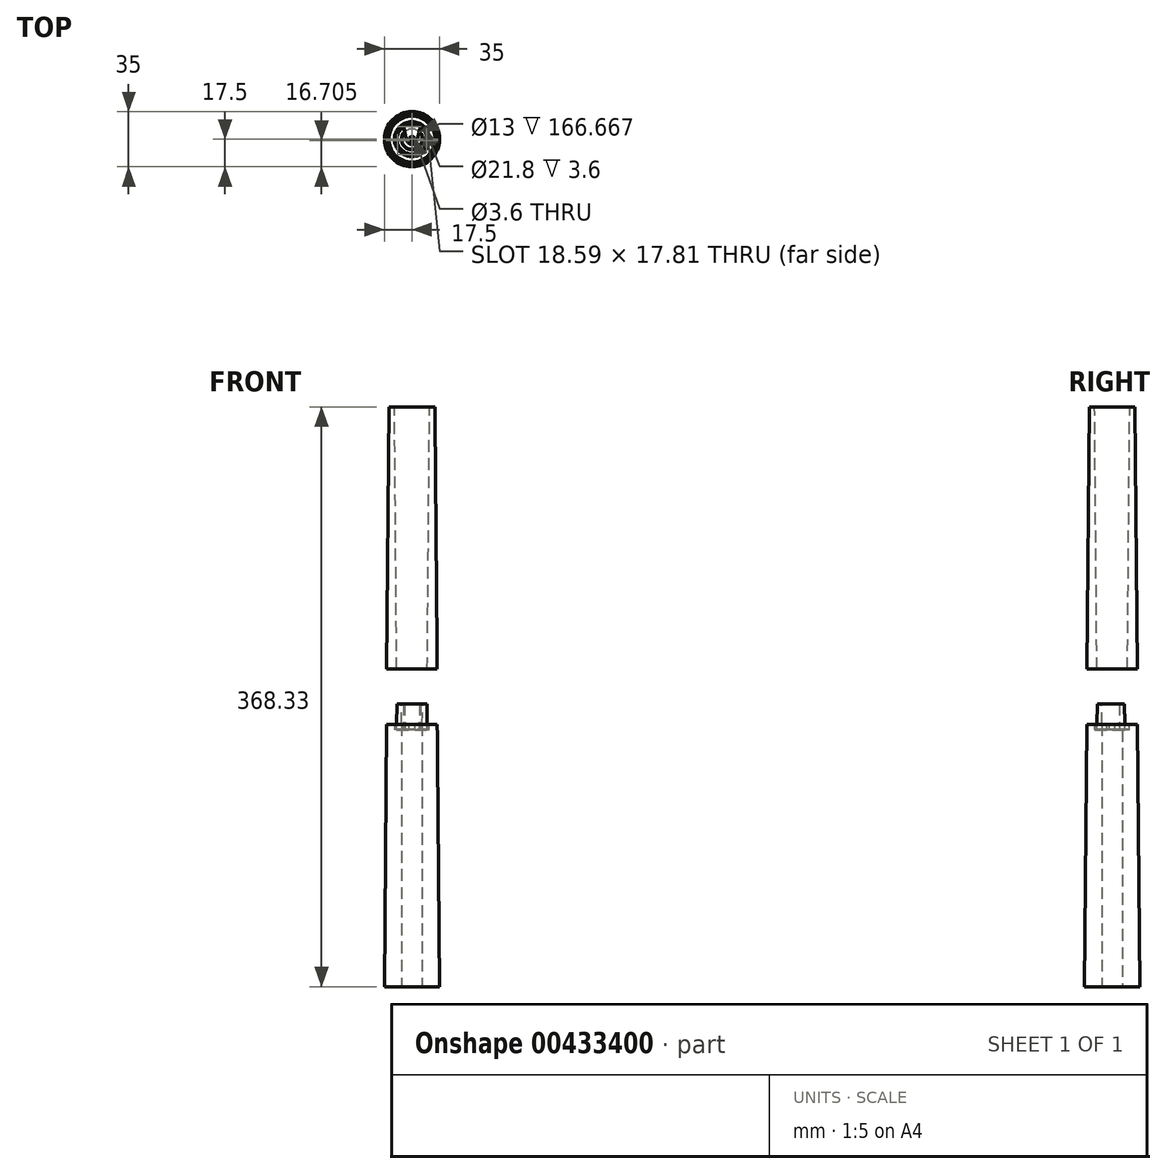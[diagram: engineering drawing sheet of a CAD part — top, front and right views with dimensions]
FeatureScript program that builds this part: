
annotation { "Feature Type Name" : "Feature", "Feature Type Description" : "" }
export const myFeature = defineFeature(function(context is Context, id is Id, definition is map)
    precondition{}
    {
        {
            assignVariable(context, id + "F0", {"name" : "RodLength", "anyValue" : 500 * mm});
        }
        {
            assignVariable(context, id + "F1", {"name" : "NubDepth", "anyValue" : 13 * mm});
        }
        {
            assignVariable(context, id + "F2", {"name" : "EjectorSupportRingDepth", "anyValue" : 3.2 * mm});
        }
        {
            var Q0;
            Q0=qCreatedBy(makeId("Top.planeOp"),FACE);
            var sketch = newSketch(context, id + "F3", { "sketchPlane" : qUnion([Q0])});
            skCircle(sketch, "E0", {"center": v(0, 0) * mm, "radius": 6.5 * mm});
            skCircle(sketch, "E1", {"center": v(0, 0) * mm, "radius": 17.5 * mm});
            skSolve(sketch);
        }
        {
            var Q0;
            Q0=qCreatedBy(makeId("Top.planeOp"),FACE);
            cPlane(context, id + "F4", {"entities" : qUnion([Q0]), "cplaneType" : CPlaneType.OFFSET, "offset" : getVariable(context, 'RodLength') / 3, "width" : 150 * mm, "height" : 150 * mm});
        }
        {
            var Q0;
            Q0=makeQuery(id+"F3.imprint","IMPRINT",FACE,{"disambiguationData":[TD([[makeQuery(id+"F3.imprint","IMPRINT",EDGE,{"derivedFrom":sQuery(id+"F3.wireOp",EDGE,"E0")}),-1.0]])]});
            var Q1;
            Q1=makeQuery(id+"F3.imprint","IMPRINT",FACE,{"disambiguationData":[TD([[makeQuery(id+"F3.imprint","IMPRINT",EDGE,{"derivedFrom":sQuery(id+"F3.wireOp",EDGE,"E0")}),1.0]])]});
            extrude(context, id + "F5", {"entities" : qUnion([Q0, Q1]), "depth" : getVariable(context, 'RodLength') / 3, "hasDraft" : true, "draftAngle" : .5 * degree, "draftPullDirection" : true});
        }
        {
            var Q0;
            Q0=makeQuery(id+"F3.imprint","IMPRINT",FACE,{"disambiguationData":[TD([[makeQuery(id+"F3.imprint","IMPRINT",EDGE,{"derivedFrom":sQuery(id+"F3.wireOp",EDGE,"E0")}),1.0]])]});
            extrude(context, id + "F6", {"entities" : qUnion([Q0]), "operationType" : NewBodyOperationType.REMOVE, "depth" : getVariable(context, 'RodLength')});
        }
        {
            var Q0;
            Q0=qCreatedBy(id+"F4.planeOp",FACE);
            var sketch = newSketch(context, id + "F7", { "sketchPlane" : qUnion([Q0])});
            skArc(sketch, "E2.0", {"start": v(-4.54, 4.65) * mm, "mid": v(0, -6.5) * mm, "end": v(4.54, 4.65) * mm});
            skCircle(sketch, "E3.0", {"center": v(0, 0) * mm, "radius": 16.05 * mm});
            skArc(sketch, "E4", {"start": v(-5.32, 8.11) * mm, "mid": v(0, -9.7) * mm, "end": v(5.32, 8.11) * mm});
            skCircle(sketch, "E5", {"center": v(0, 0) * mm, "radius": 10.9 * mm});
            skCircle(sketch, "E6", {"center": v(0, 0) * mm, "radius": 1.8 * mm});
            skArc(sketch, "E7", {"start": v(-3.32, -0.75) * mm, "mid": v(0, -3.4) * mm, "end": v(3.32, -0.75) * mm});
            skLineSegment(sketch, "E8", {"start": v(-7.1, -0.75) * mm, "end": v(9.67, -0.75) * mm, "construction": true});
            skLineSegment(sketch, "E9", {"start": v(-3.32, -0.75) * mm, "end": v(-5.32, 8.11) * mm});
            skLineSegment(sketch, "E10", {"start": v(3.32, -0.75) * mm, "end": v(5.32, 8.11) * mm});
            skSolve(sketch);
        }
        {
            var Q0;
            Q0=makeQuery(id+"F7.imprint","IMPRINT",FACE,{"disambiguationData":[TD([[makeQuery(id+"F7.imprint","IMPRINT",EDGE,{"derivedFrom":sQuery(id+"F7.wireOp",EDGE,"E2.0")}),-1.0]])]});
            extrude(context, id + "F8", {"entities" : qUnion([Q0]), "operationType" : NewBodyOperationType.ADD, "depth" : getVariable(context, 'NubDepth'), "hasDraft" : true, "draftAngle" : 1 * degree, "draftPullDirection" : true});
        }
        {
            var Q0;
            Q0=makeQuery(id+"F7.imprint","IMPRINT",FACE,{"disambiguationData":[TD([[makeQuery(id+"F7.imprint","IMPRINT",EDGE,{"derivedFrom":sQuery(id+"F7.wireOp",EDGE,"E4")}),-1.0]])]});
            extrude(context, id + "F9", {"entities" : qUnion([Q0]), "operationType" : NewBodyOperationType.REMOVE, "oppositeDirection" : true, "depth" : getVariable(context, 'EjectorSupportRingDepth') + .4 * mm});
        }
        {
            var Q0;
            {var subQ1=sQuery(id+"F7.wireOp",EDGE,"E4");Q0=makeQuery(id+"F7.imprint","IMPRINT",FACE,{"disambiguationData":[TD([[makeQuery(id+"F7.imprint","IMPRINT",EDGE,{"derivedFrom":subQ1}),-1.0]])]});}
            extrude(context, id + "F10", {"entities" : qUnion([Q0]), "oppositeDirection" : true, "depth" : getVariable(context, 'EjectorSupportRingDepth')});
        }
        {
            var Q0;
            Q0=qCreatedBy(id+"F4.planeOp",FACE);
            cPlane(context, id + "F11", {"entities" : qUnion([Q0]), "cplaneType" : CPlaneType.OFFSET, "offset" : 35 * mm, "width" : 150 * mm, "height" : 150 * mm});
        }
        {
            var Q0;
            Q0=qCreatedBy(id+"F11.planeOp",FACE);
            var sketch = newSketch(context, id + "F12", { "sketchPlane" : qUnion([Q0])});
            skCircle(sketch, "E11.0", {"center": v(0, 0) * mm, "radius": 16.05 * mm});
            skCircle(sketch, "E12.converted", {"center": v(0, 0) * mm, "radius": 9.7 * mm});
            skPoint(sketch, "E13.orphan", {"position": v(-5.32, 8.11) * mm});
            skSolve(sketch);
        }
        {
            var Q0;
            Q0=makeQuery(id+"F12.imprint","IMPRINT",FACE,{"disambiguationData":[TD([[makeQuery(id+"F12.imprint","IMPRINT",EDGE,{"derivedFrom":sQuery(id+"F12.wireOp",EDGE,"E11.0")}),1.0]])]});
            extrude(context, id + "F13", {"entities" : qUnion([Q0]), "depth" : getVariable(context, 'RodLength') / 3, "hasDraft" : true, "draftAngle" : .5 * degree, "draftPullDirection" : true});
        }
        {
            var Q0;
            Q0=makeQuery(id+"F13.opExtrude","CAP_FACE",FACE,{"disambiguationData":[OSD([sQuery(id+"F12.wireOp",EDGE,"E11.0"),sQuery(id+"F12.wireOp",EDGE,"E12.converted")])],"isStart":false});
            cPlane(context, id + "F14", {"entities" : qUnion([Q0]), "cplaneType" : CPlaneType.OFFSET, "offset" : 0 * mm, "width" : 150 * mm, "height" : 150 * mm});
        }
    });
